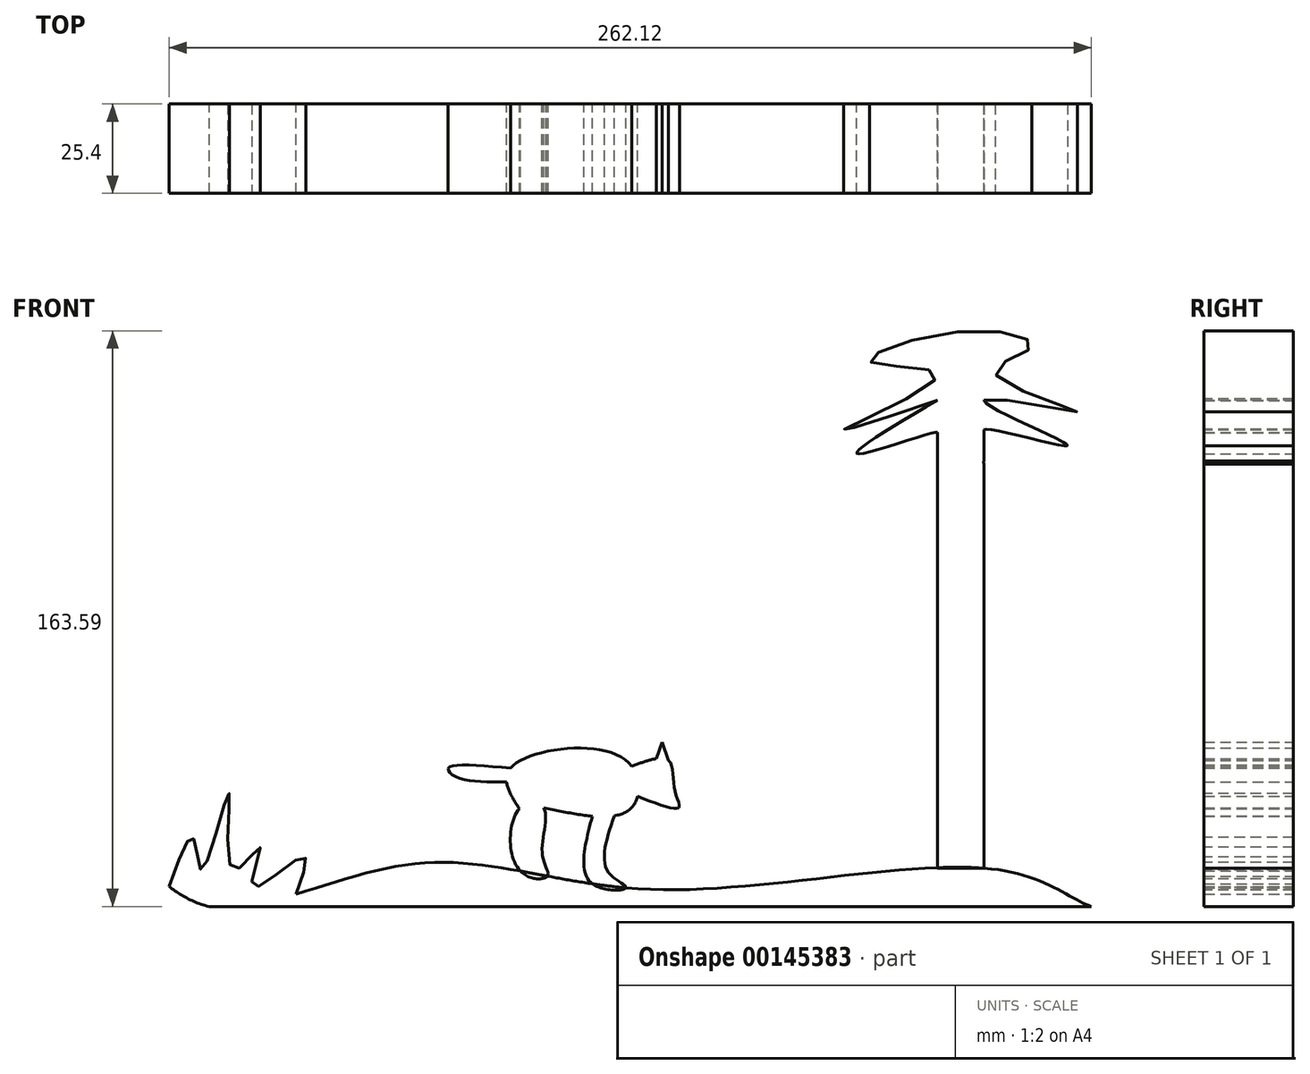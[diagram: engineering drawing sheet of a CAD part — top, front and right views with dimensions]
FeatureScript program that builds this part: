
annotation { "Feature Type Name" : "Feature", "Feature Type Description" : "" }
export const myFeature = defineFeature(function(context is Context, id is Id, definition is map)
    precondition{}
    {
        {
            var Q0;
            Q0=qCreatedBy(makeId("Front.planeOp"),FACE);
            var sketch = newSketch(context, id + "F0", { "sketchPlane" : qUnion([Q0])});
            skLineSegment(sketch, "E0", {"start": v(-148.65, -76.13) * mm, "end": v(148.65, -76.13) * mm});
            skFitSpline(sketch, "E1", {"points": [v(-148.65, -76.13) * mm, v(-129.36, -65.69) * mm, v(-108.87, -76.13) * mm, v(-51.42, -64.08) * mm, v(17.28, -71.3) * mm, v(117.71, -66.09) * mm, v(141.82, -76.13) * mm, v(148.65, -76.13) * mm], "startDerivative": vector(183.8, 156.73) * mm, "endDerivative": vector(105, 20) * mm});
            skLineSegment(sketch, "E2.bottom", {"start": v(111.28, -65.27) * mm, "end": v(98.03, -65.27) * mm});
            skLineSegment(sketch, "E2.top", {"start": v(111.28, 67.7) * mm, "end": v(98.03, 67.7) * mm});
            skLineSegment(sketch, "E2.left", {"start": v(111.28, -65.27) * mm, "end": v(111.28, 67.7) * mm});
            skLineSegment(sketch, "E2.right", {"start": v(98.03, -65.27) * mm, "end": v(98.03, 67.7) * mm});
            skFitSpline(sketch, "E3", {"points": [v(98.03, 67.7) * mm, v(75.93, 52.43) * mm, v(98.03, 58.47) * mm, v(79.14, 46.8) * mm, v(98.03, 50.04) * mm, v(79.55, 38.77) * mm, v(98.03, 38.39) * mm], "startDerivative": vector(-213.14, -125.6) * mm, "endDerivative": vector(202.55, 22.8) * mm});
            skFitSpline(sketch, "E4", {"points": [v(98.03, 67.7) * mm, v(71.91, 59.66) * mm, v(98.03, 74.95) * mm, v(79.14, 78.54) * mm, v(106.86, 87.38) * mm, v(124.54, 82.56) * mm, v(114.5, 75.33) * mm, v(137.8, 64.48) * mm, v(111.28, 67.7) * mm, v(134.99, 54.84) * mm, v(111.28, 59.28) * mm, v(131.77, 47.6) * mm, v(111.28, 50.44) * mm, v(129.36, 34.75) * mm, v(111.28, 37.99) * mm], "startDerivative": vector(-567, -192.07) * mm, "endDerivative": vector(-470.76, 140.42) * mm});
            skFitSpline(sketch, "E5", {"points": [v(-120.3, -70.47) * mm, v(-113.3, -56.85) * mm, v(-110.88, -65.69) * mm, v(-103.25, -44) * mm, v(-102.04, -65.69) * mm, v(-94.41, -59.26) * mm, v(-96.42, -70.47) * mm, v(-82.36, -62.07) * mm, v(-84.15, -72.6) * mm], "startDerivative": vector(65.7, 182.64) * mm, "endDerivative": vector(-57.14, -151.74) * mm});
            skFitSpline(sketch, "E6", {"points": [v(-20.46, -66.07) * mm, v(-12.79, -67.5) * mm, v(-14.2, -61.45) * mm, v(-13.83, -48.05) * mm, v(-20.71, -48.41) * mm, v(-20.46, -66.07) * mm]});
            skFitSpline(sketch, "E7", {"points": [v(-13.83, -48.05) * mm, v(11.16, -48.05) * mm, v(8.63, -33.92) * mm, v(-23.25, -36.82) * mm, v(-20.71, -48.41) * mm], "startDerivative": vector(111.53, -23.89) * mm, "endDerivative": vector(41.45, -64.98) * mm});
            skFitSpline(sketch, "E8", {"points": [v(0, -50.48) * mm, v(0, -69.7) * mm, v(9.56, -70.83) * mm, v(4.64, -66.52) * mm, v(6.21, -50.38) * mm], "startDerivative": vector(-20.54, -78.36) * mm, "endDerivative": vector(22.5, 66.71) * mm});
            skFitSpline(sketch, "E9", {"points": [v(12.89, -44.87) * mm, v(24.57, -48.05) * mm, v(23.48, -43.34) * mm, v(21.67, -34.65) * mm, v(11.16, -36.3) * mm], "startDerivative": vector(55.18, -21.2) * mm, "endDerivative": vector(-47.8, -17.68) * mm});
            skFitSpline(sketch, "E10", {"points": [v(-23.25, -36.82) * mm, v(-40.89, -36.82) * mm, v(-38.7, -39.3) * mm, v(-24.38, -40.72) * mm], "startDerivative": vector(-58.7, 5.36) * mm, "endDerivative": vector(43.01, 0.4) * mm});
            skLineSegment(sketch, "E11", {"start": v(18.22, -34.11) * mm, "end": v(19.9, -29.42) * mm});
            skLineSegment(sketch, "E12", {"start": v(19.9, -29.42) * mm, "end": v(21.67, -34.65) * mm});
            skSolve(sketch);
        }
        {
            var Q0;
            {var subQ4=sQuery(id+"F0.wireOp",EDGE,"E5");Q0=makeQuery(id+"F0.imprint","IMPRINT",FACE,{"disambiguationData":[TD([[makeQuery(id+"F0.imprint","IMPRINT",EDGE,{"derivedFrom":subQ4}),-1.0]])]});}
            var Q1;
            {var subQ9=sQuery(id+"F0.wireOp",EDGE,"E2.bottom");Q1=makeQuery(id+"F0.imprint","IMPRINT",FACE,{"disambiguationData":[TD([[makeQuery(id+"F0.imprint","IMPRINT",EDGE,{"derivedFrom":subQ9}),1.0]])]});}
            var Q2;
            {var subQ10=sQuery(id+"F0.wireOp",EDGE,"E2.top");Q2=makeQuery(id+"F0.imprint","IMPRINT",FACE,{"disambiguationData":[TD([[makeQuery(id+"F0.imprint","IMPRINT",EDGE,{"derivedFrom":subQ10}),1.0]])]});}
            var Q3;
            {var subQ0=sQuery(id+"F0.wireOp",EDGE,"E2.top");Q3=makeQuery(id+"F0.imprint","IMPRINT",FACE,{"disambiguationData":[TD([[makeQuery(id+"F0.imprint","IMPRINT",EDGE,{"derivedFrom":subQ0}),-1.0]])]});}
            var Q4;
            {var subQ0=sQuery(id+"F0.wireOp",EDGE,"E1");var subQ1=sQuery(id+"F0.wireOp",EDGE,"E0");var subQ2=makeQuery(id+"F0.imprint","INTERSECT",VERTEX,{"disambiguationData":[OD(0.0)],"derivedFrom":[subQ1,subQ0]});Q4=makeQuery(id+"F0.imprint","IMPRINT",FACE,{"disambiguationData":[TD([[makeQuery(id+"F0.imprint","IMPRINT",EDGE,{"disambiguationData":[TD([[subQ2,-1.0]])],"derivedFrom":subQ1}),1.0]])]});}
            var Q5;
            {var subQ0=sQuery(id+"F0.wireOp",EDGE,"E3");var subQ1=sQuery(id+"F0.wireOp",EDGE,"E2.right");var subQ2=makeQuery(id+"F0.imprint","INTERSECT",VERTEX,{"disambiguationData":[OD(0.0)],"derivedFrom":[subQ1,subQ0]});Q5=makeQuery(id+"F0.imprint","IMPRINT",FACE,{"disambiguationData":[TD([[makeQuery(id+"F0.imprint","IMPRINT",EDGE,{"disambiguationData":[TD([[subQ2,-1.0]])],"derivedFrom":subQ1}),1.0]])]});}
            var Q6;
            {var subQ0=sQuery(id+"F0.wireOp",EDGE,"E3");var subQ1=sQuery(id+"F0.wireOp",EDGE,"E2.right");var subQ2=makeQuery(id+"F0.imprint","INTERSECT",VERTEX,{"disambiguationData":[OD(2.0)],"derivedFrom":[subQ1,subQ0]});Q6=makeQuery(id+"F0.imprint","IMPRINT",FACE,{"disambiguationData":[TD([[makeQuery(id+"F0.imprint","IMPRINT",EDGE,{"disambiguationData":[TD([[subQ2,-1.0]])],"derivedFrom":subQ1}),1.0]])]});}
            var Q7;
            {var subQ0=sQuery(id+"F0.wireOp",EDGE,"E3");var subQ1=sQuery(id+"F0.wireOp",EDGE,"E2.right");var subQ3=makeQuery(id+"F0.imprint","INTERSECT",VERTEX,{"disambiguationData":[OD(4.0)],"derivedFrom":[subQ1,subQ0]});Q7=makeQuery(id+"F0.imprint","IMPRINT",FACE,{"disambiguationData":[TD([[makeQuery(id+"F0.imprint","IMPRINT",EDGE,{"disambiguationData":[TD([[subQ3,-1.0]])],"derivedFrom":subQ1}),1.0]])]});}
            var Q8;
            {var subQ0=sQuery(id+"F0.wireOp",EDGE,"E4");var subQ1=sQuery(id+"F0.wireOp",EDGE,"E2.left");var subQ2=makeQuery(id+"F0.imprint","INTERSECT",VERTEX,{"disambiguationData":[OD(4.0)],"derivedFrom":[subQ1,subQ0]});Q8=makeQuery(id+"F0.imprint","IMPRINT",FACE,{"disambiguationData":[TD([[makeQuery(id+"F0.imprint","IMPRINT",EDGE,{"disambiguationData":[TD([[subQ2,-1.0]])],"derivedFrom":subQ1}),-1.0]])]});}
            var Q9;
            {var subQ0=sQuery(id+"F0.wireOp",EDGE,"E4");var subQ1=sQuery(id+"F0.wireOp",EDGE,"E2.left");var subQ2=makeQuery(id+"F0.imprint","INTERSECT",VERTEX,{"disambiguationData":[OD(2.0)],"derivedFrom":[subQ1,subQ0]});Q9=makeQuery(id+"F0.imprint","IMPRINT",FACE,{"disambiguationData":[TD([[makeQuery(id+"F0.imprint","IMPRINT",EDGE,{"disambiguationData":[TD([[subQ2,-1.0]])],"derivedFrom":subQ1}),-1.0]])]});}
            var Q10;
            {var subQ0=sQuery(id+"F0.wireOp",EDGE,"E4");var subQ1=sQuery(id+"F0.wireOp",EDGE,"E2.left");var subQ2=makeQuery(id+"F0.imprint","INTERSECT",VERTEX,{"disambiguationData":[OD(0.0)],"derivedFrom":[subQ1,subQ0]});Q10=makeQuery(id+"F0.imprint","IMPRINT",FACE,{"disambiguationData":[TD([[makeQuery(id+"F0.imprint","IMPRINT",EDGE,{"disambiguationData":[TD([[subQ2,-1.0]])],"derivedFrom":subQ1}),-1.0]])]});}
            var Q11;
            {var subQ1=sQuery(id+"F0.wireOp",EDGE,"E7");var subQ9=makeQuery(id+"F0.imprint","IMPRINT",VERTEX,{"derivedFrom":subQ1});Q11=makeQuery(id+"F0.imprint","IMPRINT",FACE,{"disambiguationData":[TD([[makeQuery(id+"F0.imprint","IMPRINT",EDGE,{"disambiguationData":[TD([[subQ9,1.0]])],"derivedFrom":subQ1}),1.0]])]});}
            var Q12;
            {var subQ0=sQuery(id+"F0.wireOp",EDGE,"E6");var subQ1=sQuery(id+"F0.wireOp",EDGE,"E1");var subQ2=makeQuery(id+"F0.imprint","INTERSECT",VERTEX,{"disambiguationData":[OD(0.0)],"derivedFrom":[subQ1,subQ0]});Q12=makeQuery(id+"F0.imprint","IMPRINT",FACE,{"disambiguationData":[TD([[makeQuery(id+"F0.imprint","IMPRINT",EDGE,{"disambiguationData":[TD([[subQ2,-1.0]])],"derivedFrom":subQ1}),1.0]])]});}
            var Q13;
            {var subQ0=sQuery(id+"F0.wireOp",EDGE,"E8");var subQ1=sQuery(id+"F0.wireOp",EDGE,"E1");var subQ2=makeQuery(id+"F0.imprint","INTERSECT",VERTEX,{"disambiguationData":[OD(0.0)],"derivedFrom":[subQ1,subQ0]});Q13=makeQuery(id+"F0.imprint","IMPRINT",FACE,{"disambiguationData":[TD([[makeQuery(id+"F0.imprint","IMPRINT",EDGE,{"disambiguationData":[TD([[subQ2,1.0]])],"derivedFrom":subQ1}),1.0]])]});}
            var Q14;
            {var subQ0=sQuery(id+"F0.wireOp",EDGE,"E9");var subQ4=makeQuery(id+"F0.imprint","IMPRINT",VERTEX,{"derivedFrom":subQ0});Q14=makeQuery(id+"F0.imprint","IMPRINT",FACE,{"disambiguationData":[TD([[makeQuery(id+"F0.imprint","IMPRINT",EDGE,{"disambiguationData":[TD([[subQ4,1.0]])],"derivedFrom":subQ0}),1.0]])]});}
            var Q15;
            {var subQ1=sQuery(id+"F0.wireOp",EDGE,"E7");var subQ6=sQuery(id+"F0.wireOp",EDGE,"E6");var subQ7=makeQuery(id+"F0.imprint","INTERSECT",VERTEX,{"disambiguationData":[OD(0.0)],"derivedFrom":[subQ6,subQ1]});Q15=makeQuery(id+"F0.imprint","IMPRINT",FACE,{"disambiguationData":[TD([[makeQuery(id+"F0.imprint","IMPRINT",EDGE,{"disambiguationData":[TD([[subQ7,-1.0]])],"derivedFrom":subQ6}),-1.0]])]});}
            var Q16;
            {var subQ0=sQuery(id+"F0.wireOp",EDGE,"E10");Q16=makeQuery(id+"F0.imprint","IMPRINT",FACE,{"disambiguationData":[TD([[makeQuery(id+"F0.imprint","IMPRINT",EDGE,{"derivedFrom":subQ0}),1.0]])]});}
            var Q17;
            {var subQ0=sQuery(id+"F0.wireOp",EDGE,"E9");var subQ1=sQuery(id+"F0.wireOp",EDGE,"E7");var subQ2=makeQuery(id+"F0.imprint","INTERSECT",VERTEX,{"disambiguationData":[OD(0.0)],"derivedFrom":[subQ1,subQ0]});Q17=makeQuery(id+"F0.imprint","IMPRINT",FACE,{"disambiguationData":[TD([[makeQuery(id+"F0.imprint","IMPRINT",EDGE,{"disambiguationData":[TD([[subQ2,-1.0]])],"derivedFrom":subQ1}),-1.0]])]});}
            var Q18;
            {var subQ0=sQuery(id+"F0.wireOp",EDGE,"E11");Q18=makeQuery(id+"F0.imprint","IMPRINT",FACE,{"disambiguationData":[TD([[makeQuery(id+"F0.imprint","IMPRINT",EDGE,{"derivedFrom":subQ0}),-1.0]])]});}
            extrude(context, id + "F1", {"entities" : qUnion([Q0, Q1, Q2, Q3, Q4, Q5, Q6, Q7, Q8, Q9, Q10, Q11, Q12, Q13, Q14, Q15, Q16, Q17, Q18]), "endBound" : BoundingType.SYMMETRIC, "depth" : 25.4 * mm});
        }
    });
